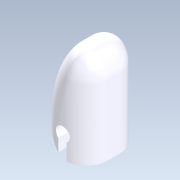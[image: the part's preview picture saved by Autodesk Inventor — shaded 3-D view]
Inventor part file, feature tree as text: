
AUTODESK INVENTOR PART (.ipt)
format: ipt  version: 2020.2 (Build 242310000, 310)  size: 279,552 bytes
history: native  units: mm
features: extrude x4, sketch x3, fillet x2
ambient origin geometry x8: Origin, YZ Plane, XZ Plane, XY Plane, X Axis, Y Axis, Z Axis, Center Point
bodies: Solid1 (feature_tree)
feature tree (9):
  extrude  "Extrusion1"  Depth=25.0mm
  extrude  "Extrusion2"  Depth=17.0mm
  fillet  "Fillet1"  Radius=17.0mm
  fillet  "Fillet2"  Radius=2.5mm
  extrude  "Extrusion5"  TaperAngle=135.0deg  [1 undecoded]
  extrude  "Extrusion6"  Depth=20.0mm TaperAngle=0.0deg
  sketch  "Sketch2"  dims[d1=2.5mm d2=25.0mm]
  sketch  "Sketch5"  dims[d3=5.0mm d5=17.0mm d9=17.0mm d10=2.5mm]
  sketch  "Sketch6"  dims[d11=0.0mm d13=135.0deg d14=20.0mm d15=0.0mm d16=8.0mm d17=5.0mm d18=1.5mm d19=3.0mm d24=0.0mm d25=0.0mm d26=8.0mm d36=4.0mm d37=2.0mm d38=2.0mm d39=0.0mm d40=0.0mm d41=19.0mm d42=6.5mm d43=20.009mm d44=0.0mm d45=0.5mm d46=0.872665mm]
note: 1 required parameter value undecoded (feature->parameter linkage not recoverable at this tier; creation-order binding heuristic only, values carry confidence <= 0.55)
